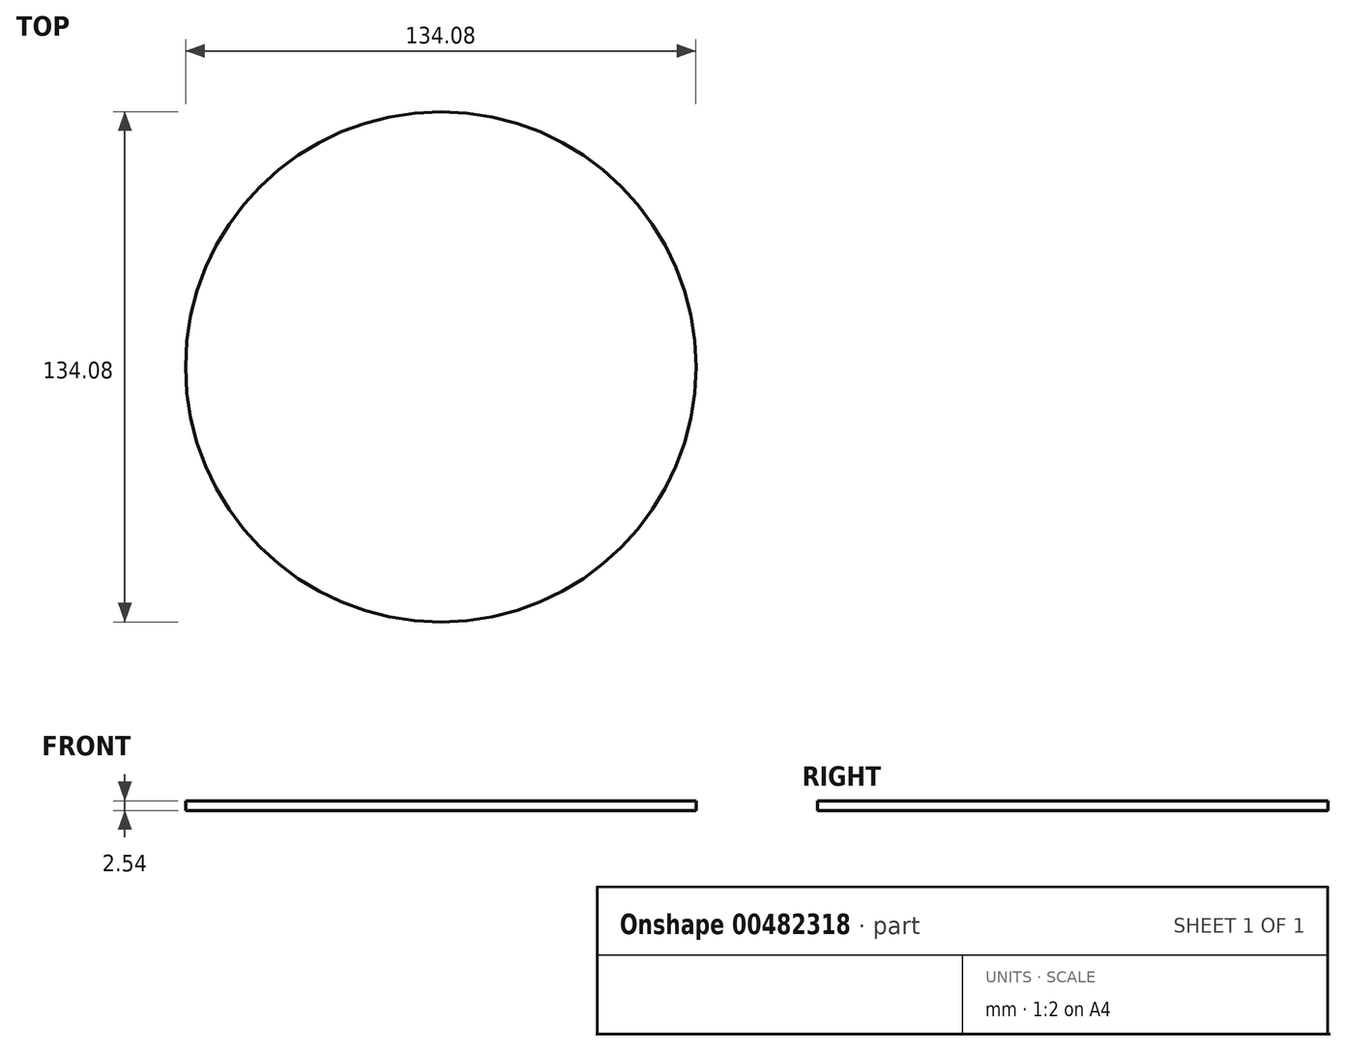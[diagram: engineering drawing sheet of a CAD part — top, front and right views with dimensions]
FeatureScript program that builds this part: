
annotation { "Feature Type Name" : "Feature", "Feature Type Description" : "" }
export const myFeature = defineFeature(function(context is Context, id is Id, definition is map)
    precondition{}
    {
        {
            var Q0;
            Q0=qCreatedBy(makeId("Top.planeOp"),FACE);
            var sketch = newSketch(context, id + "F0", { "sketchPlane" : qUnion([Q0])});
            skCircle(sketch, "E0", {"center": v(0, 0) * mm, "radius": 67.04 * mm});
            skSolve(sketch);
        }
        {
            var Q0;
            Q0 = qSketchRegion(id + "F0", true);
            extrude(context, id + "F1", {"entities" : qUnion([Q0]), "oppositeDirection" : true, "depth" : 2.54 * mm});
        }
    });
